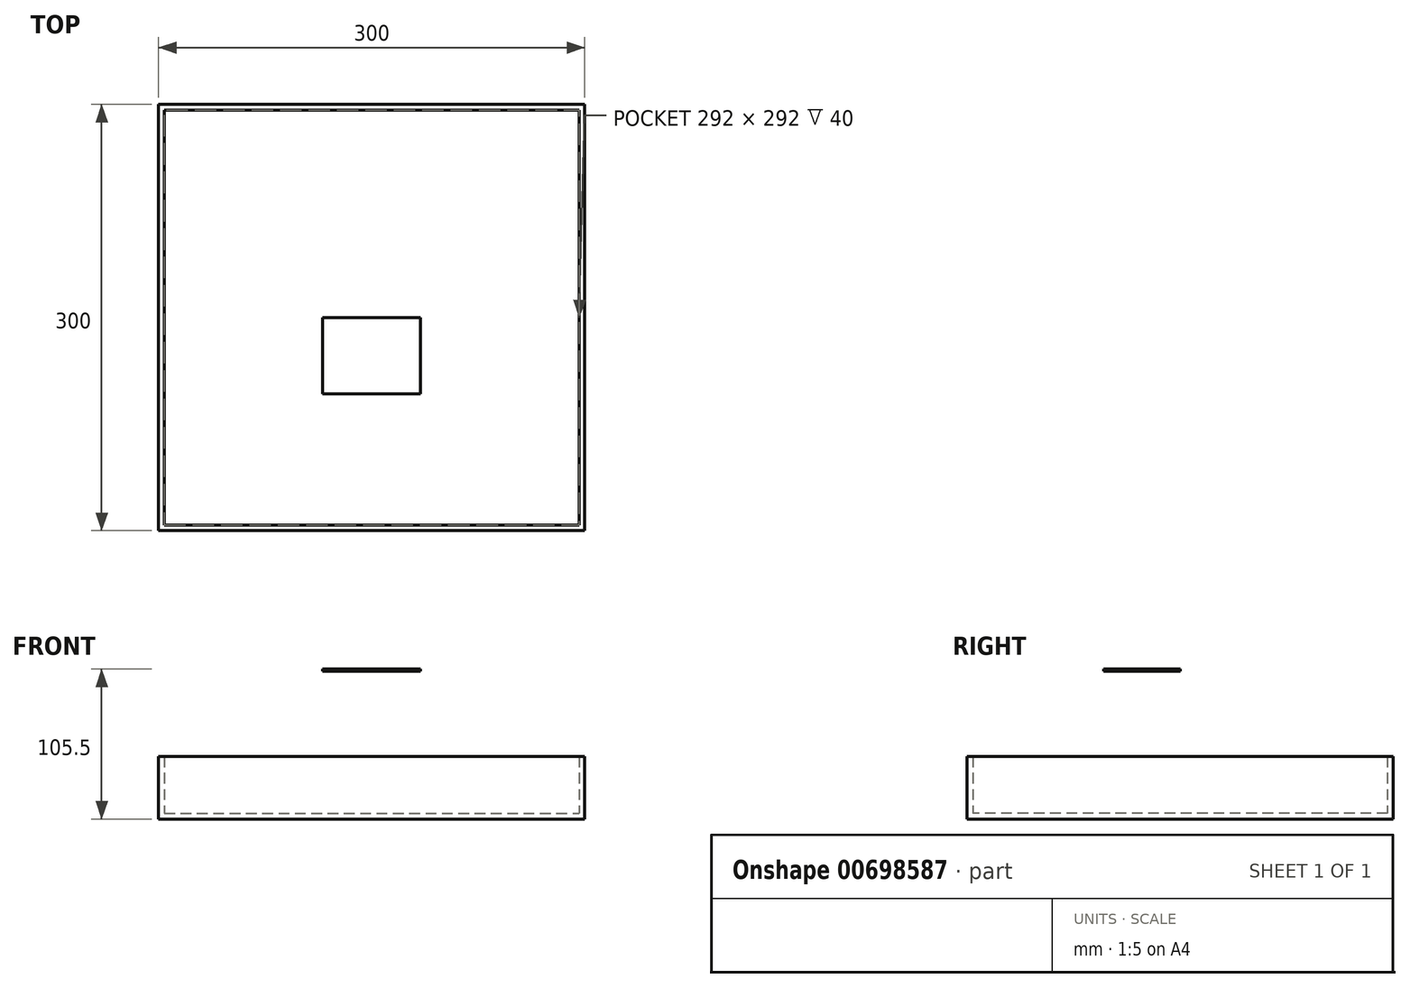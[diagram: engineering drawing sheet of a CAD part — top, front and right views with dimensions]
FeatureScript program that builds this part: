
annotation { "Feature Type Name" : "Feature", "Feature Type Description" : "" }
export const myFeature = defineFeature(function(context is Context, id is Id, definition is map)
    precondition{}
    {
        {
            var Q0;
            Q0=qCreatedBy(makeId("Top.planeOp"),FACE);
            var sketch = newSketch(context, id + "F0", { "sketchPlane" : qUnion([Q0])});
            skLineSegment(sketch, "E0.bottom", {"start": v(-150, 150) * mm, "end": v(150, 150) * mm});
            skLineSegment(sketch, "E0.top", {"start": v(-150, -150) * mm, "end": v(150, -150) * mm});
            skLineSegment(sketch, "E0.left", {"start": v(-150, 150) * mm, "end": v(-150, -150) * mm});
            skLineSegment(sketch, "E0.right", {"start": v(150, 150) * mm, "end": v(150, -150) * mm});
            skLineSegment(sketch, "E1", {"start": v(0, 150) * mm, "end": v(0, -150) * mm, "construction": true});
            skLineSegment(sketch, "E2", {"start": v(-150, 0) * mm, "end": v(150, 0) * mm, "construction": true});
            skSolve(sketch);
        }
        {
            var Q0;
            Q0 = qSketchRegion(id + "F0", true);
            extrude(context, id + "F1", {"entities" : qUnion([Q0]), "depth" : 4 * mm, "offsetDistance" : 25 * mm});
        }
        {
            var Q0;
            Q0=makeQuery(id+"F1.opExtrude","CAP_FACE",FACE,{"disambiguationData":[OSD([sQuery(id+"F0.wireOp",EDGE,"E0.bottom"),sQuery(id+"F0.wireOp",EDGE,"E0.top"),sQuery(id+"F0.wireOp",EDGE,"E0.left"),sQuery(id+"F0.wireOp",EDGE,"E0.right")])],"isStart":false});
            var sketch = newSketch(context, id + "F2", { "sketchPlane" : qUnion([Q0])});
            skLineSegment(sketch, "E3.bottom", {"start": v(-150, 150) * mm, "end": v(150, 150) * mm});
            skLineSegment(sketch, "E3.top", {"start": v(-150, -150) * mm, "end": v(150, -150) * mm});
            skLineSegment(sketch, "E3.left", {"start": v(-150, 150) * mm, "end": v(-150, -150) * mm});
            skLineSegment(sketch, "E3.right", {"start": v(150, 150) * mm, "end": v(150, -150) * mm});
            skLineSegment(sketch, "E4.bottom", {"start": v(-146, 146) * mm, "end": v(146, 146) * mm});
            skLineSegment(sketch, "E4.top", {"start": v(-146, -146) * mm, "end": v(146, -146) * mm});
            skLineSegment(sketch, "E4.left", {"start": v(-146, 146) * mm, "end": v(-146, -146) * mm});
            skLineSegment(sketch, "E4.right", {"start": v(146, 146) * mm, "end": v(146, -146) * mm});
            skSolve(sketch);
        }
        {
            var Q0;
            Q0=makeQuery(id+"F2.imprint","IMPRINT",FACE,{"disambiguationData":[TD([[makeQuery(id+"F2.imprint","IMPRINT",EDGE,{"derivedFrom":sQuery(id+"F2.wireOp",EDGE,"E3.bottom")}),-1.0]])]});
            extrude(context, id + "F3", {"entities" : qUnion([Q0]), "operationType" : NewBodyOperationType.ADD, "depth" : 40 * mm, "offsetDistance" : 25 * mm});
        }
        {
            var Q0;
            Q0=qCreatedBy(makeId("Front.planeOp"),FACE);
            var sketch = newSketch(context, id + "F4", { "sketchPlane" : qUnion([Q0])});
            skLineSegment(sketch, "E5.bottom", {"start": v(-34.45, 105.5) * mm, "end": v(34.45, 105.5) * mm});
            skLineSegment(sketch, "E5.top", {"start": v(-34.45, 104) * mm, "end": v(34.45, 104) * mm});
            skLineSegment(sketch, "E5.left", {"start": v(-34.45, 105.5) * mm, "end": v(-34.45, 104) * mm});
            skLineSegment(sketch, "E5.right", {"start": v(34.45, 105.5) * mm, "end": v(34.45, 104) * mm});
            skSolve(sketch);
        }
        {
            var Q0;
            Q0=makeQuery(id+"F4.imprint","IMPRINT",FACE,{"disambiguationData":[TD([[makeQuery(id+"F4.imprint","IMPRINT",EDGE,{"derivedFrom":sQuery(id+"F4.wireOp",EDGE,"E5.bottom")}),-1.0]])]});
            extrude(context, id + "F5", {"entities" : qUnion([Q0]), "depth" : 53.8 * mm, "offsetDistance" : 25 * mm});
        }
    });
